# Revit family: 2069358 Sylvania Lighting Fixture PIXER RECESSED 600X600 HE 4P TW SSC01
name_source: partatom
category: Lighting Fixtures
revit_build: Autodesk Revit 2016 (Build: 20150220_1215(x64)
units: mm (PartAtom-declared; Revit-internal decimal feet)

## family parameters
Cut with Voids When Loaded = No
Host = Face
Light Source = No
OmniClass Number = 23.80.70.00
OmniClass Title = Lighting
Part Type = Normal
Room Calculation Point = No
Round Connector Dimension = Use Diameter
Shared = No

## types (1)
- 2069358 PIXER R 600 HE 4P TW SSC01
    Apparent Load = 32 VA
    Assembly Code = D5020200
    AssetType = Fixed
    ClassificationName = Uniclass2015
    ClassificationValue = EF_70_80
    Cost = 0 $
    Default Elevation = 1219 mm
    Description = PIXER RECESSED 600X600 HE 4P TW SSC01
    DocumentationLiterature = http://www.sylvania-lighting.com
    IfcExportAs = 106
    IfcExportType = IfcLightFixtureType
    ImpactProtectionIndex = Class II
    InputNominalFrequency = IK02
    InputVoltage = IP20
    Keynote = 0
    LampMacAdamStep = 16500
    LampNominalLuminous = LED
    Length_SYL = 595 mm  [stored 1.9521 ft]
    LightOutputRatio = 3
    LuminaireType = 3400 lm
    LuminousEfficacy = 100
    Material_1_SYL = PC/ABS Plastic
    Model = PIXER RECESSED 600X600 HE 4P TW SSC01
    ModelNumber = 2069358
    ModelReference = PIXER RECESSED 600X600 HE 4P TW SSC01
    Name = PIXER RECESSED 600X600 HE 4P TW SSC01
    NominalDepth = 595 mm  [stored 1.9521 ft]
    NominalHeight = 75 mm
    NominalLength = 595 mm  [stored 1.9521 ft]
    PodXInstance_SYL = 2
    PowerConsumption = 595
    PowerFactor = 0
    RadiusBody_SYL = 5 mm  [stored 0.0164042 ft]
    Type Image = <None>
    TypeName = PIXER RECESSED 600X600 HE 4P TW SSC01
    TypePodSQ_SYL = Pixer Pod Square : PIXER
    URL = 2069358.ies
    Voltage = 230 V
    WarrantyDescription = 0.96
    WarrantyDurationUnit = http://www.sylvania-lighting.com
    Width_SYL = 595 mm  [stored 1.9521 ft]
    Xdistance_SYL = 149 mm
    Xinstance_SYL = 4
    Ydistance_SYL = 149 mm
    Yinstance_SYL = 4

note: [stored X ft] marks values corroborated as IEEE doubles in the binary element streams (Revit-internal decimal feet)

## geometry (parser evidence)
native form markers: Sweep x4
no freeform markers — native parametric forms only
